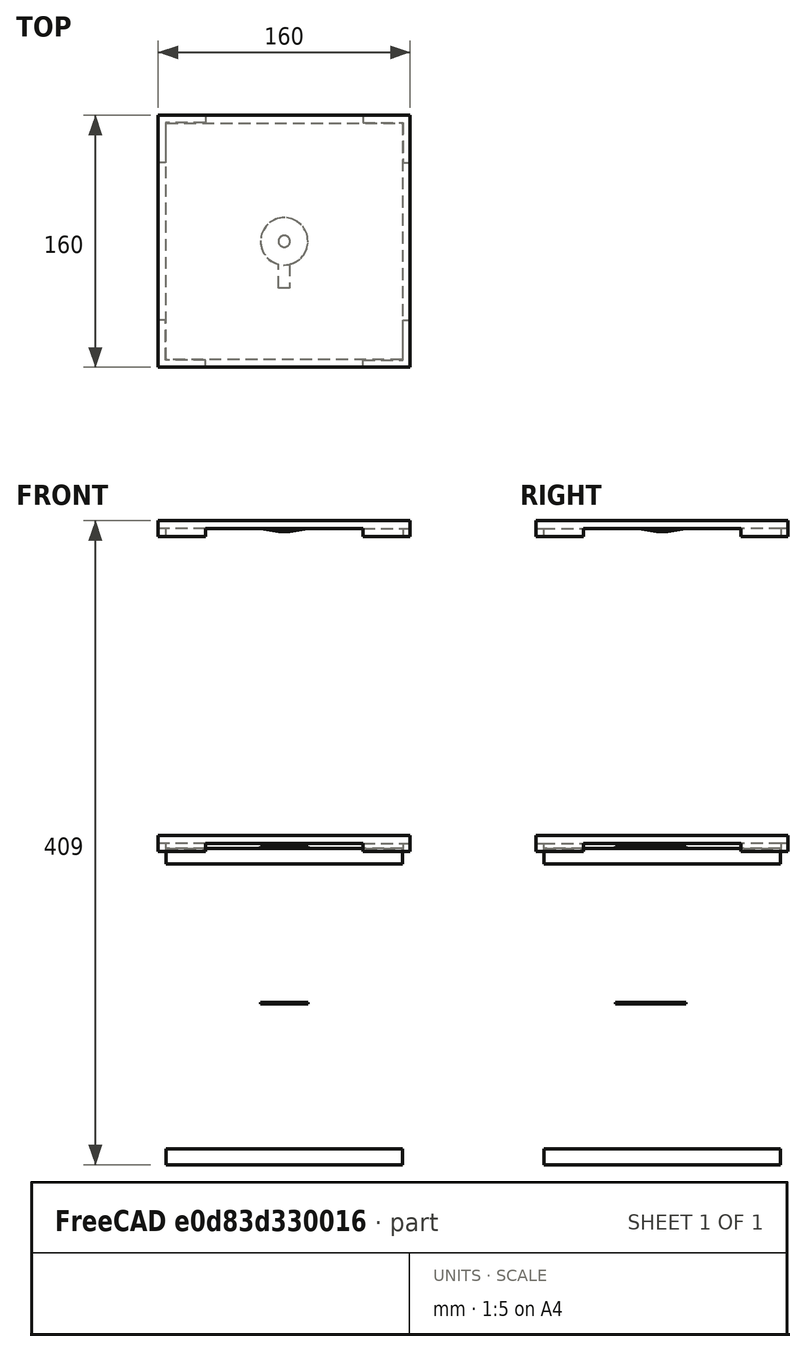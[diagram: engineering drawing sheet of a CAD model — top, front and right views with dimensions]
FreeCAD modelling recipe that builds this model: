
FCSTD DOCUMENT  (FreeCAD 0.21R33771 (Git))
Label: Pedle
License: All rights reserved
LicenseURL: https://en.wikipedia.org/wiki/All_rights_reserved
objects: Sketcher::SketchObject×10, PartDesign::Pad×10, TechDraw::DrawProjGroupItem×10, TechDraw::DrawViewDimension×10, PartDesign::Body×6, Part::Mirroring×6, TechDraw::DrawProjGroup×4, TechDraw::DrawSVGTemplate×3, TechDraw::DrawPage×3, TechDraw::DrawViewBalloon×3, App::DocumentObjectGroupPython×3, PartDesign::Draft×2, Part::MultiFuse×2, App::Part×2, Part::Feature×2, Spreadsheet::Sheet×1, TechDraw::DrawViewSpreadsheet×1
note: 67 computed .brp shape members not serialized (recipe doc carries the construction recipe); baked Part::Feature solids carry a one-line shape summary decoded from their .brp

FEATURE [Sketcher::SketchObject] Sketch
  FullyConstrained = true
  MapMode = 5
  Support = -> [XY_Plane]
  sketch-geometry (5):
    g0: LineSegment StartX=-75 StartY=-75 StartZ=0 EndX=-75 EndY=75 EndZ=0
    g1: LineSegment StartX=-75 StartY=75 StartZ=0 EndX=75 EndY=75 EndZ=0
    g2: LineSegment StartX=75 StartY=75 StartZ=0 EndX=75 EndY=-75 EndZ=0
    g3: LineSegment StartX=75 StartY=-75 StartZ=0 EndX=-75 EndY=-75 EndZ=0
    g4: GeomPoint X=-6e-16 Y=0 Z=0
  constraints (12):
    c: Coincident(g0,g1)
    c: Coincident(g1,g2)
    c: Coincident(g2,g3)
    c: Coincident(g3,g0)
    c: Horizontal(g1)
    c: Horizontal(g3)
    c: Vertical(g0)
    c: Vertical(g2)
    c: Symmetric(g1,g0,g4)
    c: Coincident(g4,g-1)
    c: Equal(g1,g2)
    c: DistanceX(g1,g1) = 150
FEATURE [PartDesign::Pad] Pad
  Direction = (0,0,1)
  Length = 10
  Length2 = 10
  Profile = -> Sketch
  ReferenceAxis = -> Sketch [N_Axis]
  Reversed = true
  Type = 0
FEATURE [PartDesign::Body] Body  label="Foam"
  Group = -> [Sketch,Pad]
  Origin = -> Origin
  Placement = pos=(0,0,-3) rot=(0,0,1;0rad)
  Tip = -> Pad
FEATURE [Sketcher::SketchObject] Sketch001
  FullyConstrained = true
  MapMode = 5
  Support = -> [XY_Plane001]
  sketch-geometry (4):
    g0: LineSegment StartX=-80 StartY=0 StartZ=0 EndX=-80 EndY=80 EndZ=0
    g1: LineSegment StartX=-80 StartY=80 StartZ=0 EndX=0 EndY=80 EndZ=0
    g2: LineSegment StartX=0 StartY=80 StartZ=0 EndX=0 EndY=0 EndZ=0
    g3: LineSegment StartX=0 StartY=0 StartZ=0 EndX=-80 EndY=0 EndZ=0
  constraints (11):
    c: Coincident(g0,g1)
    c: Coincident(g1,g2)
    c: Coincident(g2,g3)
    c: Coincident(g3,g0)
    c: Horizontal(g1)
    c: Horizontal(g3)
    c: Vertical(g0)
    c: Vertical(g2)
    c: DistanceX(g1,g1) = 80
    c: Equal(g2,g1)
    c: Coincident(g2,g-1)
FEATURE [PartDesign::Pad] Pad001
  Direction = (0,0,1)
  Length = 5
  Length2 = 10
  Profile = -> Sketch001
  ReferenceAxis = -> Sketch001 [N_Axis]
  Type = 0
FEATURE [Sketcher::SketchObject] Sketch002
  FullyConstrained = true
  MapMode = 5
  Support = -> [XY_Plane001]
  expr: Constraints[11] = Sketch.Constraints[11]
  expr: Constraints[20] = Sketch001.Constraints[8]
  sketch-geometry (15):
    g0: LineSegment StartX=-75 StartY=-75 StartZ=0 EndX=-75 EndY=75 EndZ=0
    g1: LineSegment StartX=-75 StartY=75 StartZ=0 EndX=75 EndY=75 EndZ=0
    g2: LineSegment StartX=75 StartY=75 StartZ=0 EndX=75 EndY=-75 EndZ=0
    g3: LineSegment StartX=75 StartY=-75 StartZ=0 EndX=-75 EndY=-75 EndZ=0
    g4: GeomPoint X=0 Y=0 Z=0
    g5: LineSegment StartX=-80 StartY=0 StartZ=0 EndX=-80 EndY=80 EndZ=0
    g6: LineSegment StartX=-80 StartY=80 StartZ=0 EndX=0 EndY=80 EndZ=0
    g7: LineSegment StartX=0 StartY=80 StartZ=0 EndX=0 EndY=0 EndZ=0
    g8: LineSegment StartX=0 StartY=0 StartZ=0 EndX=-80 EndY=0 EndZ=0
    g9: LineSegment StartX=-80 StartY=80 StartZ=0 EndX=-50 EndY=80 EndZ=0
    g10: LineSegment StartX=-50 StartY=80 StartZ=0 EndX=-50 EndY=75.4 EndZ=0
    g11: LineSegment StartX=-50 StartY=75.4 StartZ=0 EndX=-75.4 EndY=75.4 EndZ=0
    g12: LineSegment StartX=-75.4 StartY=75.4 StartZ=0 EndX=-75.4 EndY=50 EndZ=0
    g13: LineSegment StartX=-75.4 StartY=50 StartZ=0 EndX=-80 EndY=50 EndZ=0
    g14: LineSegment StartX=-80 StartY=50 StartZ=0 EndX=-80 EndY=80 EndZ=0
  constraints (40):
    c: Coincident(g0,g1)
    c: Coincident(g1,g2)
    c: Coincident(g2,g3)
    c: Coincident(g3,g0)
    c: Horizontal(g1)
    c: Horizontal(g3)
    c: Vertical(g0)
    c: Vertical(g2)
    c: Symmetric(g1,g0,g4)
    c: Coincident(g4,g-1)
    c: Equal(g1,g2)
    c: DistanceX(g1,g1) = 150
    c: Coincident(g5,g6)
    c: Coincident(g6,g7)
    c: Coincident(g7,g8)
    c: Coincident(g8,g5)
    c: Horizontal(g6)
    c: Horizontal(g8)
    c: Vertical(g5)
    c: Vertical(g7)
    c: DistanceX(g6,g6) = 80
    c: Equal(g7,g6)
    c: Coincident(g7,g-1)
    c: Coincident(g9,g5)
    c: PointOnObject(g9,g6)
    c: Coincident(g10,g9)
    c: Vertical(g10)
    c: Coincident(g11,g10)
    c: Horizontal(g11)
    c: Coincident(g12,g11)
    c: Vertical(g12)
    c: Coincident(g13,g12)
    c: PointOnObject(g13,g5)
    c: Horizontal(g13)
    c: Coincident(g14,g13)
    c: Coincident(g14,g9)
    c: Equal(g9,g14)
    c: Equal(g13,g10)
    c: DistanceX(g11,g0) = 0.4
    c: DistanceX(g9,g9) = 30
FEATURE [PartDesign::Pad] Pad002
  BaseFeature = -> Pad001
  Direction = (0,0,1)
  Length = 5
  Length2 = 10
  Profile = -> Sketch002
  ReferenceAxis = -> Sketch002 [N_Axis]
  Reversed = true
  Type = 0
  expr: Length = 5
FEATURE [Sketcher::SketchObject] Sketch003
  FullyConstrained = true
  MapMode = 5
  Support = -> [XY_Plane001]
  sketch-geometry (3):
    g0: ArcOfCircle CenterX=0 CenterY=0 CenterZ=0 NormalX=0 NormalY=0 NormalZ=1 AngleXU=0 Radius=15 StartAngle=1.5708 EndAngle=3.14159
    g1: LineSegment StartX=9e-16 StartY=15 StartZ=0 EndX=0 EndY=0 EndZ=0
    g2: LineSegment StartX=0 StartY=0 StartZ=0 EndX=-15 EndY=1.8e-15 EndZ=0
  constraints (8):
    c: Coincident(g0,g-1)
    c: PointOnObject(g0,g-2)
    c: PointOnObject(g0,g-1)
    c: Radius(g0) = 15
    c: Coincident(g1,g0)
    c: Coincident(g1,g0)
    c: Coincident(g2,g0)
    c: Coincident(g2,g0)
FEATURE [PartDesign::Pad] Pad003
  BaseFeature = -> Pad002
  Direction = (0,0,1)
  Length = 2
  Length2 = 10
  Profile = -> Sketch003
  ReferenceAxis = -> Sketch003 [N_Axis]
  Reversed = true
  Type = 0
FEATURE [PartDesign::Draft] Draft
  Angle = 80
  Base = -> Pad003 [Face14]
  BaseFeature = -> Pad003
  NeutralPlane = -> Pad003 [Face4]
  Reversed = true
  SupportTransform = false
FEATURE [PartDesign::Body] Body001  label="HardPart"
  Group = -> [Sketch001,Pad001,Sketch002,Pad002,Sketch003,Pad003,Draft]
  Origin = -> Origin001
  Tip = -> Draft
FEATURE [Part::Mirroring] Part__Mirroring  label="HardPart (Mirror #1)"
  Base = (0,0,0)
  Normal = (0,1,0)
  Source = -> Body001
FEATURE [Part::Mirroring] Part__Mirroring001  label="HardPart (Mirror #2)"
  Base = (0,0,0)
  Normal = (1,0,0)
  Source = -> Part__Mirroring
FEATURE [Part::Mirroring] Part__Mirroring002  label="HardPart (Mirror #3)"
  Base = (0,0,0)
  Normal = (1,0,0)
  Source = -> Body001
FEATURE [Part::MultiFuse] Fusion
  Placement = pos=(0,0,200) rot=(0,0,1;0rad)
  Shapes = -> [Part__Mirroring,Part__Mirroring001,Part__Mirroring002,Body001]
FEATURE [Sketcher::SketchObject] Sketch004
  FullyConstrained = true
  MapMode = 5
  Support = -> [XY_Plane002]
  sketch-geometry (4):
    g0: ArcOfCircle CenterX=0 CenterY=0 CenterZ=0 NormalX=0 NormalY=0 NormalZ=1 AngleXU=0 Radius=15 StartAngle=4.94789 EndAngle=10.7601
    g1: LineSegment StartX=3.5 StartY=-14.586 StartZ=0 EndX=3.5 EndY=-29.586 EndZ=0
    g2: LineSegment StartX=3.5 StartY=-29.586 StartZ=0 EndX=-3.5 EndY=-29.586 EndZ=0
    g3: LineSegment StartX=-3.5 StartY=-29.586 StartZ=0 EndX=-3.5 EndY=-14.586 EndZ=0
  constraints (11):
    c: Coincident(g0,g-1)
    c: Coincident(g1,g0)
    c: Vertical(g1)
    c: Coincident(g2,g1)
    c: Coincident(g3,g2)
    c: Coincident(g3,g0)
    c: Vertical(g3)
    c: Symmetric(g1,g2,g-2)
    c: Radius(g0) = 15
    c: DistanceY(g1,g1) = 15
    c: DistanceX(g2,g2) = 7
FEATURE [PartDesign::Pad] Pad004
  Direction = (0,0,1)
  Length = 1
  Length2 = 10
  Placement = pos=(0,0,100) rot=(0,0,1;0rad)
  Profile = -> Sketch004
  ReferenceAxis = -> Sketch004 [N_Axis]
  Type = 0
FEATURE [PartDesign::Body] Body002  label="Sensor"
  Group = -> [Sketch004,Pad004]
  Origin = -> Origin002
  Placement = pos=(0,0,-3) rot=(0,0,1;0rad)
  Tip = -> Pad004
FEATURE [TechDraw::DrawSVGTemplate] Template
  EditableTexts = AuthorName=Alex Anastasakis; CheckDate=2024/11/11; CreationDate=2024/11/11; DrawingNumber=1; FC-Scale=1:2; FC-Title=Plate; SheetNumber=1 of 1; Subtitle=Course: Industrial Design for Game Hardware; SupervisorName=Alvaro Uribe Quevedo; Weight=0.09
  Height = 297
  Orientation = 1
  Template = C:/Program Files/FreeCAD 0.21/data/Mod/TechDraw/Templates/A3_LandscapeTD.svg
  Width = 420
FEATURE [TechDraw::DrawProjGroupItem] ProjItem  label="Front"
  CoarseView = false
  Direction = (0,-1,0)
  Focus = 100
  HardHidden = false
  IsoCount = 0
  IsoHidden = false
  IsoVisible = false
  LockPosition = true
  Perspective = false
  Rotation = 0
  RotationVector = (1,0,0)
  Scale = 0.5
  ScaleType = 2
  ScrubCount = 0
  SeamHidden = false
  SeamVisible = false
  SmoothHidden = false
  SmoothVisible = true
  Source = -> [Fusion]
  Type = 0
  X = 0
  XDirection = (1,0,0)
  Y = 0
FEATURE [TechDraw::DrawProjGroupItem] ProjItem001  label="Bottom"
  CoarseView = false
  Direction = (0,0,-1)
  Focus = 100
  HardHidden = false
  IsoCount = 0
  IsoHidden = false
  IsoVisible = false
  LockPosition = false
  Perspective = false
  Rotation = 0
  RotationVector = (1,0,0)
  Scale = 0.5
  ScaleType = 2
  ScrubCount = 0
  SeamHidden = false
  SeamVisible = false
  SmoothHidden = false
  SmoothVisible = true
  Source = -> [Fusion]
  Type = 5
  X = 0
  XDirection = (1,0,0)
  Y = -72.5
FEATURE [TechDraw::DrawViewDimension] Dimension002
  AngleOverride = false
  Arbitrary = false
  ArbitraryTolerances = false
  EqualTolerance = true
  ExtensionAngle = 0
  FormatSpec = ⌀%.2w
  FormatSpecOverTolerance = %+.2w
  FormatSpecUnderTolerance = %+.2w
  Inverted = false
  LineAngle = 0
  LockPosition = false
  MeasureType = 1
  OverTolerance = 0
  References2D = -> [ProjItem001]
  Rotation = 0
  Scale = 0.5
  ScaleType = 0
  TheoreticalExact = false
  Type = 5
  UnderTolerance = 0
  X = 51.6169
  Y = 21.7849
FEATURE [TechDraw::DrawViewDimension] Dimension003
  AngleOverride = false
  Arbitrary = false
  ArbitraryTolerances = false
  EqualTolerance = true
  ExtensionAngle = 0
  FormatSpec = %.2w
  FormatSpecOverTolerance = %+.2w
  FormatSpecUnderTolerance = %+.2w
  Inverted = false
  LineAngle = 0
  LockPosition = false
  MeasureType = 1
  OverTolerance = 0
  References2D = -> [ProjItem]
  Rotation = 0
  Scale = 0.5
  ScaleType = 0
  TheoreticalExact = false
  Type = 2
  UnderTolerance = 0
  X = -57.1938
  Y = 16.266
FEATURE [TechDraw::DrawViewDimension] Dimension004
  AngleOverride = false
  Arbitrary = false
  ArbitraryTolerances = false
  EqualTolerance = true
  ExtensionAngle = 0
  FormatSpec = %.2w
  FormatSpecOverTolerance = %+.2w
  FormatSpecUnderTolerance = %+.2w
  Inverted = false
  LineAngle = 0
  LockPosition = false
  MeasureType = 1
  OverTolerance = 0
  References2D = -> [ProjItem]
  Rotation = 0
  Scale = 0.5
  ScaleType = 0
  TheoreticalExact = false
  Type = 2
  UnderTolerance = 0
  X = -48.3522
  Y = 16.1652
FEATURE [TechDraw::DrawViewDimension] Dimension005
  AngleOverride = false
  Arbitrary = false
  ArbitraryTolerances = false
  EqualTolerance = true
  ExtensionAngle = 0
  FormatSpec = %.2w x80°
  FormatSpecOverTolerance = %+.2w
  FormatSpecUnderTolerance = %+.2w
  Inverted = false
  LineAngle = 0
  LockPosition = false
  MeasureType = 1
  OverTolerance = 0
  References2D = -> [ProjItem]
  Rotation = 0
  Scale = 0.5
  ScaleType = 0
  TheoreticalExact = false
  Type = 2
  UnderTolerance = 0
  X = 52.4746
  Y = 12.9587
FEATURE [TechDraw::DrawProjGroupItem] ProjItem002  label="FrontTopRight"
  CoarseView = false
  Direction = (0.57735,-0.57735,0.57735)
  Focus = 100
  HardHidden = false
  IsoCount = 0
  IsoHidden = false
  IsoVisible = false
  LockPosition = false
  Perspective = false
  Rotation = 0
  RotationVector = (1,0,0)
  ScaleType = 2
  ScrubCount = 0
  SeamHidden = false
  SeamVisible = false
  SmoothHidden = false
  SmoothVisible = true
  Source = -> [Fusion]
  Type = 7
  X = 126.569
  XDirection = (0.707107,0.707107,0)
  Y = 72.5
FEATURE [TechDraw::DrawProjGroupItem] ProjItem003  label="Top"
  CoarseView = false
  Direction = (0,0,1)
  Focus = 100
  HardHidden = false
  IsoCount = 0
  IsoHidden = false
  IsoVisible = false
  LockPosition = false
  Perspective = false
  Rotation = 0
  RotationVector = (1,0,0)
  ScaleType = 2
  ScrubCount = 0
  SeamHidden = false
  SeamVisible = false
  SmoothHidden = false
  SmoothVisible = true
  Source = -> [Fusion]
  Type = 4
  X = 0
  XDirection = (1,0,0)
  Y = 72.5
FEATURE [TechDraw::DrawProjGroup] ProjGroup
  Anchor = -> ProjItem
  AutoDistribute = true
  LockPosition = false
  ProjectionType = 1
  Rotation = 0
  Scale = 0.5
  ScaleType = 0
  Source = -> [Fusion]
  Views = -> [ProjItem,ProjItem001,ProjItem002,ProjItem003]
  X = 155.738
  Y = 152.297
  spacingX = 30
  spacingY = 30
FEATURE [TechDraw::DrawViewDimension] Dimension
  AngleOverride = false
  Arbitrary = false
  ArbitraryTolerances = false
  EqualTolerance = true
  ExtensionAngle = 0
  FormatSpec = %.2w
  FormatSpecOverTolerance = %+.2w
  FormatSpecUnderTolerance = %+.2w
  Inverted = false
  LineAngle = 0
  LockPosition = false
  MeasureType = 1
  OverTolerance = 0
  References2D = -> [ProjItem003]
  Rotation = 0
  Scale = 0.5
  ScaleType = 0
  TheoreticalExact = false
  Type = 1
  UnderTolerance = 0
  X = -0.816766
  Y = 56.5615
FEATURE [TechDraw::DrawViewDimension] Dimension006
  AngleOverride = false
  Arbitrary = false
  ArbitraryTolerances = false
  EqualTolerance = true
  ExtensionAngle = 0
  FormatSpec = %.2w
  FormatSpecOverTolerance = %+.2w
  FormatSpecUnderTolerance = %+.2w
  Inverted = false
  LineAngle = 0
  LockPosition = false
  MeasureType = 1
  OverTolerance = 0
  References2D = -> [ProjItem003]
  Rotation = 0
  Scale = 0.5
  ScaleType = 0
  TheoreticalExact = false
  Type = 2
  UnderTolerance = 0
  X = -53.9399
  Y = 2.24418
FEATURE [TechDraw::DrawViewDimension] Dimension007
  AngleOverride = false
  Arbitrary = false
  ArbitraryTolerances = false
  EqualTolerance = true
  ExtensionAngle = 0
  FormatSpec = %.2w
  FormatSpecOverTolerance = %+.2w
  FormatSpecUnderTolerance = %+.2w
  Inverted = false
  LineAngle = 0
  LockPosition = false
  MeasureType = 1
  OverTolerance = 0
  References2D = -> [ProjItem001]
  Rotation = 0
  Scale = 0.5
  ScaleType = 0
  TheoreticalExact = false
  Type = 1
  UnderTolerance = 0
  X = -51.8082
  Y = 18.2692
FEATURE [TechDraw::DrawViewDimension] Dimension008
  AngleOverride = false
  Arbitrary = false
  ArbitraryTolerances = false
  EqualTolerance = true
  ExtensionAngle = 0
  FormatSpec = %.2w
  FormatSpecOverTolerance = %+.2w
  FormatSpecUnderTolerance = %+.2w
  Inverted = false
  LineAngle = 0
  LockPosition = false
  MeasureType = 1
  OverTolerance = 0
  References2D = -> [ProjItem001]
  Rotation = 0
  Scale = 0.5
  ScaleType = 0
  TheoreticalExact = false
  Type = 2
  UnderTolerance = 0
  X = -14.7786
  Y = 52.5746
FEATURE [TechDraw::DrawViewDimension] Dimension009
  AngleOverride = false
  Arbitrary = false
  ArbitraryTolerances = false
  EqualTolerance = true
  ExtensionAngle = 0
  FormatSpec = %.2w
  FormatSpecOverTolerance = %+.2w
  FormatSpecUnderTolerance = %+.2w
  Inverted = false
  LineAngle = 0
  LockPosition = false
  MeasureType = 1
  OverTolerance = 0
  References2D = -> [ProjItem001]
  Rotation = 0
  Scale = 0.5
  ScaleType = 0
  TheoreticalExact = false
  Type = 2
  UnderTolerance = 0
  X = -59.7622
  Y = 10.7657
FEATURE [TechDraw::DrawViewDimension] Dimension010
  AngleOverride = false
  Arbitrary = false
  ArbitraryTolerances = false
  EqualTolerance = true
  ExtensionAngle = 0
  FormatSpec = %.2w
  FormatSpecOverTolerance = %+.2w
  FormatSpecUnderTolerance = %+.2w
  Inverted = false
  LineAngle = 0
  LockPosition = false
  MeasureType = 1
  OverTolerance = 0
  References2D = -> [ProjItem001]
  Rotation = 0
  Scale = 0.5
  ScaleType = 0
  TheoreticalExact = false
  Type = 1
  UnderTolerance = 0
  X = -5.20054
  Y = 58.7965
FEATURE [TechDraw::DrawPage] Page
  KeepUpdated = true
  NextBalloonIndex = 1
  ProjectionType = 0
  Scale = 0.5
  Template = -> Template
  Views = -> [ProjGroup,Dimension002,Dimension003,Dimension004,Dimension005,Dimension,Dimension006,Dimension007,Dimension008,Dimension009,Dimension010]
FEATURE [App::Part] Part  label="Pedal"
  Group = -> [Body,Part__Mirroring002,Part__Mirroring001,Part__Mirroring,Body001,Fusion,Body002]
  Origin = -> Origin003
FEATURE [Sketcher::SketchObject] Sketch005
  FullyConstrained = true
  MapMode = 5
  Support = -> [XY_Plane004]
  sketch-geometry (5):
    g0: LineSegment StartX=-75 StartY=-75 StartZ=0 EndX=-75 EndY=75 EndZ=0
    g1: LineSegment StartX=-75 StartY=75 StartZ=0 EndX=75 EndY=75 EndZ=0
    g2: LineSegment StartX=75 StartY=75 StartZ=0 EndX=75 EndY=-75 EndZ=0
    g3: LineSegment StartX=75 StartY=-75 StartZ=0 EndX=-75 EndY=-75 EndZ=0
    g4: GeomPoint X=-6e-16 Y=0 Z=0
  constraints (12):
    c: Coincident(g0,g1)
    c: Coincident(g1,g2)
    c: Coincident(g2,g3)
    c: Coincident(g3,g0)
    c: Horizontal(g1)
    c: Horizontal(g3)
    c: Vertical(g0)
    c: Vertical(g2)
    c: Symmetric(g1,g0,g4)
    c: Coincident(g4,g-1)
    c: Equal(g1,g2)
    c: DistanceX(g1,g1) = 150
FEATURE [PartDesign::Pad] Pad005
  Direction = (0,0,1)
  Length = 10
  Length2 = 10
  Profile = -> Sketch005
  ReferenceAxis = -> Sketch005 [N_Axis]
  Reversed = true
  Type = 0
FEATURE [PartDesign::Body] Body003  label="Foam001"
  Group = -> [Sketch005,Pad005]
  Origin = -> Origin004
  Placement = pos=(0,0,-194) rot=(0,0,1;0rad)
  Tip = -> Pad005
FEATURE [Sketcher::SketchObject] Sketch006
  FullyConstrained = true
  MapMode = 5
  Support = -> [XY_Plane005]
  sketch-geometry (4):
    g0: LineSegment StartX=-80 StartY=0 StartZ=0 EndX=-80 EndY=80 EndZ=0
    g1: LineSegment StartX=-80 StartY=80 StartZ=0 EndX=0 EndY=80 EndZ=0
    g2: LineSegment StartX=0 StartY=80 StartZ=0 EndX=0 EndY=0 EndZ=0
    g3: LineSegment StartX=0 StartY=0 StartZ=0 EndX=-80 EndY=0 EndZ=0
  constraints (11):
    c: Coincident(g0,g1)
    c: Coincident(g1,g2)
    c: Coincident(g2,g3)
    c: Coincident(g3,g0)
    c: Horizontal(g1)
    c: Horizontal(g3)
    c: Vertical(g0)
    c: Vertical(g2)
    c: DistanceX(g1,g1) = 80
    c: Equal(g2,g1)
    c: Coincident(g2,g-1)
FEATURE [PartDesign::Pad] Pad006
  Direction = (0,0,1)
  Length = 5
  Length2 = 10
  Profile = -> Sketch006
  ReferenceAxis = -> Sketch006 [N_Axis]
  Type = 0
FEATURE [Sketcher::SketchObject] Sketch007
  FullyConstrained = true
  MapMode = 5
  Support = -> [XY_Plane005]
  expr: Constraints[11] = Sketch005.Constraints[11]
  expr: Constraints[20] = Sketch006.Constraints[8]
  sketch-geometry (15):
    g0: LineSegment StartX=-75 StartY=-75 StartZ=0 EndX=-75 EndY=75 EndZ=0
    g1: LineSegment StartX=-75 StartY=75 StartZ=0 EndX=75 EndY=75 EndZ=0
    g2: LineSegment StartX=75 StartY=75 StartZ=0 EndX=75 EndY=-75 EndZ=0
    g3: LineSegment StartX=75 StartY=-75 StartZ=0 EndX=-75 EndY=-75 EndZ=0
    g4: GeomPoint X=0 Y=0 Z=0
    g5: LineSegment StartX=-80 StartY=0 StartZ=0 EndX=-80 EndY=80 EndZ=0
    g6: LineSegment StartX=-80 StartY=80 StartZ=0 EndX=0 EndY=80 EndZ=0
    g7: LineSegment StartX=0 StartY=80 StartZ=0 EndX=0 EndY=0 EndZ=0
    g8: LineSegment StartX=0 StartY=0 StartZ=0 EndX=-80 EndY=0 EndZ=0
    g9: LineSegment StartX=-80 StartY=80 StartZ=0 EndX=-50 EndY=80 EndZ=0
    g10: LineSegment StartX=-50 StartY=80 StartZ=0 EndX=-50 EndY=75.4 EndZ=0
    g11: LineSegment StartX=-50 StartY=75.4 StartZ=0 EndX=-75.4 EndY=75.4 EndZ=0
    g12: LineSegment StartX=-75.4 StartY=75.4 StartZ=0 EndX=-75.4 EndY=50 EndZ=0
    g13: LineSegment StartX=-75.4 StartY=50 StartZ=0 EndX=-80 EndY=50 EndZ=0
    g14: LineSegment StartX=-80 StartY=50 StartZ=0 EndX=-80 EndY=80 EndZ=0
  constraints (40):
    c: Coincident(g0,g1)
    c: Coincident(g1,g2)
    c: Coincident(g2,g3)
    c: Coincident(g3,g0)
    c: Horizontal(g1)
    c: Horizontal(g3)
    c: Vertical(g0)
    c: Vertical(g2)
    c: Symmetric(g1,g0,g4)
    c: Coincident(g4,g-1)
    c: Equal(g1,g2)
    c: DistanceX(g1,g1) = 150
    c: Coincident(g5,g6)
    c: Coincident(g6,g7)
    c: Coincident(g7,g8)
    c: Coincident(g8,g5)
    c: Horizontal(g6)
    c: Horizontal(g8)
    c: Vertical(g5)
    c: Vertical(g7)
    c: DistanceX(g6,g6) = 80
    c: Equal(g7,g6)
    c: Coincident(g7,g-1)
    c: Coincident(g9,g5)
    c: PointOnObject(g9,g6)
    c: Coincident(g10,g9)
    c: Vertical(g10)
    c: Coincident(g11,g10)
    c: Horizontal(g11)
    c: Coincident(g12,g11)
    c: Vertical(g12)
    c: Coincident(g13,g12)
    c: PointOnObject(g13,g5)
    c: Horizontal(g13)
    c: Coincident(g14,g13)
    c: Coincident(g14,g9)
    c: Equal(g9,g14)
    c: Equal(g13,g10)
    c: DistanceX(g11,g0) = 0.4
    c: DistanceX(g9,g9) = 30
FEATURE [PartDesign::Pad] Pad007
  BaseFeature = -> Pad006
  Direction = (0,0,1)
  Length = 5
  Length2 = 10
  Profile = -> Sketch007
  ReferenceAxis = -> Sketch007 [N_Axis]
  Reversed = true
  Type = 0
  expr: Length = 5
FEATURE [Sketcher::SketchObject] Sketch008
  FullyConstrained = true
  MapMode = 5
  Support = -> [XY_Plane005]
  sketch-geometry (3):
    g0: ArcOfCircle CenterX=0 CenterY=0 CenterZ=0 NormalX=0 NormalY=0 NormalZ=1 AngleXU=0 Radius=15 StartAngle=1.5708 EndAngle=3.14159
    g1: LineSegment StartX=9e-16 StartY=15 StartZ=0 EndX=0 EndY=0 EndZ=0
    g2: LineSegment StartX=0 StartY=0 StartZ=0 EndX=-15 EndY=1.8e-15 EndZ=0
  constraints (8):
    c: Coincident(g0,g-1)
    c: PointOnObject(g0,g-2)
    c: PointOnObject(g0,g-1)
    c: Radius(g0) = 15
    c: Coincident(g1,g0)
    c: Coincident(g1,g0)
    c: Coincident(g2,g0)
    c: Coincident(g2,g0)
FEATURE [PartDesign::Pad] Pad008
  BaseFeature = -> Pad007
  Direction = (0,0,1)
  Length = 2
  Length2 = 10
  Profile = -> Sketch008
  ReferenceAxis = -> Sketch008 [N_Axis]
  Reversed = true
  Type = 0
FEATURE [PartDesign::Draft] Draft001
  Angle = 80
  Base = -> Pad008 [Face14]
  BaseFeature = -> Pad008
  NeutralPlane = -> Pad008 [Face4]
  Reversed = true
  SupportTransform = false
FEATURE [PartDesign::Body] Body004  label="HardPart001"
  Group = -> [Sketch006,Pad006,Sketch007,Pad007,Sketch008,Pad008,Draft001]
  Origin = -> Origin005
  Tip = -> Draft001
FEATURE [Part::Mirroring] Part__Mirroring003  label="HardPart (Mirror #1)001"
  Base = (0,0,0)
  Normal = (0,1,0)
  Source = -> Body004
FEATURE [Part::Mirroring] Part__Mirroring004  label="HardPart (Mirror #2)001"
  Base = (0,0,0)
  Normal = (1,0,0)
  Source = -> Part__Mirroring003
FEATURE [Part::Mirroring] Part__Mirroring005  label="HardPart (Mirror #3)001"
  Base = (0,0,0)
  Normal = (1,0,0)
  Source = -> Body004
FEATURE [Part::MultiFuse] Fusion001
  Shapes = -> [Part__Mirroring003,Part__Mirroring004,Part__Mirroring005,Body004]
FEATURE [Sketcher::SketchObject] Sketch009
  FullyConstrained = true
  MapMode = 5
  Support = -> [XY_Plane006]
  sketch-geometry (4):
    g0: ArcOfCircle CenterX=0 CenterY=0 CenterZ=0 NormalX=0 NormalY=0 NormalZ=1 AngleXU=0 Radius=15 StartAngle=4.94789 EndAngle=10.7601
    g1: LineSegment StartX=3.5 StartY=-14.586 StartZ=0 EndX=3.5 EndY=-29.586 EndZ=0
    g2: LineSegment StartX=3.5 StartY=-29.586 StartZ=0 EndX=-3.5 EndY=-29.586 EndZ=0
    g3: LineSegment StartX=-3.5 StartY=-29.586 StartZ=0 EndX=-3.5 EndY=-14.586 EndZ=0
  constraints (11):
    c: Coincident(g0,g-1)
    c: Coincident(g1,g0)
    c: Vertical(g1)
    c: Coincident(g2,g1)
    c: Coincident(g3,g2)
    c: Coincident(g3,g0)
    c: Vertical(g3)
    c: Symmetric(g1,g2,g-2)
    c: Radius(g0) = 15
    c: DistanceY(g1,g1) = 15
    c: DistanceX(g2,g2) = 7
FEATURE [PartDesign::Pad] Pad009
  Direction = (0,0,1)
  Length = 1
  Length2 = 10
  Profile = -> Sketch009
  ReferenceAxis = -> Sketch009 [N_Axis]
  Type = 0
FEATURE [PartDesign::Body] Body005  label="Sensor001"
  Group = -> [Sketch009,Pad009]
  Origin = -> Origin006
  Placement = pos=(0,0,-102) rot=(0,0,1;0rad)
  Tip = -> Pad009
FEATURE [App::Part] Part001  label="PedalExploded"
  Group = -> [Body003,Part__Mirroring005,Part__Mirroring004,Part__Mirroring003,Body004,Fusion001,Body005]
  Origin = -> Origin007
FEATURE [TechDraw::DrawSVGTemplate] Template001
  EditableTexts = AuthorName=Alex Anastasakis; CheckDate=2024/11/11; CreationDate=2024/11/11; FC-Scale=1:2; FC-Title=Pedal; SheetNumber=1 of 1; Subtitle=Course: Industrial Design for Game Hardware; SupervisorName=Alvaro Uribe Quevedo
  Height = 297
  Orientation = 1
  Template = C:/Program Files/FreeCAD 0.21/data/Mod/TechDraw/Templates/A3_LandscapeTD.svg
  Width = 420
FEATURE [TechDraw::DrawProjGroupItem] ProjItem004  label="Front001"
  CoarseView = false
  Direction = (0.57735,-0.57735,0.57735)
  Focus = 100
  HardHidden = false
  IsoCount = 0
  IsoHidden = false
  IsoVisible = false
  LockPosition = true
  Perspective = false
  Rotation = 0
  RotationVector = (0.707107,0.707107,0)
  Scale = 0.5
  ScaleType = 2
  ScrubCount = 0
  SeamHidden = false
  SeamVisible = false
  SmoothHidden = false
  SmoothVisible = true
  Source = -> [Part001]
  Type = 0
  X = 0
  XDirection = (0.707107,0.707107,0)
  Y = 0
FEATURE [TechDraw::DrawProjGroup] ProjGroup001
  Anchor = -> ProjItem004
  AutoDistribute = true
  LockPosition = false
  ProjectionType = 1
  Rotation = 0
  Scale = 0.5
  ScaleType = 0
  Source = -> [Part001]
  Views = -> [ProjItem004]
  X = 316.321
  Y = 151.977
  spacingX = 15
  spacingY = 15
FEATURE [Spreadsheet::Sheet] Spreadsheet  label="#BOM#"
  cells = A1='PARTS LIST; A2='ITEM NO.; B2='QTY; C2='NAME; D2='PART DESCRIPTION; E2='MATERIAL; F2='COST; A3=1; B3=1; C3='Plate; D3='Hard surface; E3='PLA; F3='$22.99 (1kg of filament); A4=2; B4=1; C4='Sensor; D4='Force sensor; E4='Plastic/Metal; F4='$14.19; A5=3; B5=1; C5='Foam Pad; D5='Soft foam pad; E5='Polyethylene Foam; F5='$26.99 (pack of sheets)
FEATURE [TechDraw::DrawViewSpreadsheet] Sheet
  CellEnd = F5
  CellStart = A1
  Font = osifont
  LineWidth = 0.5
  LockPosition = false
  Rotation = 0
  ScaleType = 2
  Source = -> Spreadsheet
  Symbol = <blob: 5512 chars omitted>
  TextSize = 12
  X = 331.62
  Y = 267.089
FEATURE [TechDraw::DrawViewBalloon] Balloon
  BubbleShape = 0
  EndType = 0
  EndTypeScale = 1
  KinkLength = 5
  LockPosition = false
  OriginX = 45.5118
  OriginY = 122.624
  Rotation = 0
  Scale = 0.5
  ScaleType = 0
  ShapeScale = 1
  SourceView = -> ProjItem004
  Text = 1
  TextWrapLen = -1
  X = 150.75
  Y = 146.591
FEATURE [TechDraw::DrawViewBalloon] Balloon001
  BubbleShape = 0
  EndType = 0
  EndTypeScale = 1
  KinkLength = 5
  LockPosition = false
  OriginX = 15.1043
  OriginY = -2.32329
  Rotation = 0
  Scale = 0.5
  ScaleType = 0
  ShapeScale = 1
  SourceView = -> ProjItem004
  Text = 2
  TextWrapLen = -1
  X = 154.067
  Y = 31.5952
FEATURE [TechDraw::DrawViewBalloon] Balloon002
  BubbleShape = 0
  EndType = 0
  EndTypeScale = 1
  KinkLength = 5
  LockPosition = false
  OriginX = 68.1792
  OriginY = -57.0569
  Rotation = 0
  Scale = 0.5
  ScaleType = 0
  ShapeScale = 1
  SourceView = -> ProjItem004
  Text = 3
  TextWrapLen = -1
  X = 154.067
  Y = -44.7001
FEATURE [TechDraw::DrawProjGroupItem] ProjItem005  label="Front002"
  CoarseView = false
  Direction = (0,-1,0)
  Focus = 100
  HardHidden = false
  IsoCount = 0
  IsoHidden = false
  IsoVisible = false
  LockPosition = true
  Perspective = false
  Rotation = 0
  RotationVector = (1,0,0)
  ScaleType = 2
  ScrubCount = 0
  SeamHidden = false
  SeamVisible = false
  SmoothHidden = false
  SmoothVisible = true
  Source = -> [Part]
  Type = 0
  X = 0
  XDirection = (1,0,0)
  Y = 0
FEATURE [TechDraw::DrawProjGroupItem] ProjItem006  label="FrontBottomLeft"
  CoarseView = false
  Direction = (-0.57735,-0.57735,-0.57735)
  Focus = 100
  HardHidden = false
  IsoCount = 0
  IsoHidden = false
  IsoVisible = false
  LockPosition = false
  Perspective = false
  Rotation = 0
  RotationVector = (1,0,0)
  ScaleType = 2
  ScrubCount = 0
  SeamHidden = false
  SeamVisible = false
  SmoothHidden = false
  SmoothVisible = true
  Source = -> [Part]
  Type = 8
  X = -111.569
  XDirection = (0.707107,-0.707107,0)
  Y = -54.8135
FEATURE [TechDraw::DrawProjGroupItem] ProjItem007  label="FrontTopLeft"
  CoarseView = false
  Direction = (-0.57735,-0.57735,0.57735)
  Focus = 100
  HardHidden = false
  IsoCount = 0
  IsoHidden = false
  IsoVisible = false
  LockPosition = false
  Perspective = false
  Rotation = 0
  RotationVector = (1,0,0)
  ScaleType = 2
  ScrubCount = 0
  SeamHidden = false
  SeamVisible = false
  SmoothHidden = false
  SmoothVisible = true
  Source = -> [Part]
  Type = 6
  X = -111.569
  XDirection = (0.707107,-0.707107,0)
  Y = 54.8135
FEATURE [TechDraw::DrawProjGroup] ProjGroup002
  Anchor = -> ProjItem005
  AutoDistribute = true
  LockPosition = false
  ProjectionType = 1
  Rotation = 0
  Scale = 0.5
  ScaleType = 0
  Source = -> [Part]
  Views = -> [ProjItem005,ProjItem006,ProjItem007]
  X = 192.784
  Y = 149.92
  spacingX = 15
  spacingY = 15
FEATURE [TechDraw::DrawPage] Page001  label="Exploded"
  KeepUpdated = true
  NextBalloonIndex = 4
  ProjectionType = 0
  Scale = 0.5
  Template = -> Template001
  Views = -> [ProjGroup001,Sheet,Balloon,Balloon001,Balloon002,ProjGroup002]
FEATURE [Part::Feature] trajectory_line
  Placement = pos=(40,40,0) rot=(0,0,1;0rad)
  shape: bbox 2e-07 x 2e-07 x 200 mm, 0 faces, 0 solids (baked)
FEATURE [App::DocumentObjectGroupPython] SimpleGroup  # scripted group (container) (typed FeaturePython)
  AnimationStepTime = 0
  AnimationSteps = 80
  Distance = 200
  Group = -> [trajectory_line]
  Revolutions = 0
  dir_vectors = (1) [(0,0,1)]
  rot_centers = (1) [(-40,-40,5)]
  rot_vectors = (1) [(0,0,1)]
FEATURE [Part::Feature] trajectory_line001
  shape: bbox 2e-07 x 2e-07 x 20 mm, 0 faces, 0 solids (baked)
FEATURE [App::DocumentObjectGroupPython] SimpleGroup001  # scripted group (container) (typed FeaturePython)
  AnimationStepTime = 0
  AnimationSteps = 60
  Distance = 100
  Group = -> [trajectory_line001]
  Revolutions = 0
  dir_vectors = (1) [(0,0,1)]
  rot_centers = (1) [(-2.68016e-16,-2.82798,1)]
  rot_vectors = (1) [(0,0,1)]
FEATURE [App::DocumentObjectGroupPython] ExplodedAssembly  # scripted group (container) (typed FeaturePython)
  AnimationStep = 0
  CurrentTrajectory = -1
  Group = -> [SimpleGroup,SimpleGroup001]
  InAnimation = false
  RemoveAllTrajectories = false
  ResetAnimation = false
FEATURE [TechDraw::DrawSVGTemplate] Template002
  EditableTexts = AuthorName=AUTHOR NAME; CheckDate=CHECK DATE; CreationDate=CREATION DATE; DrawingNumber=NUMBER; FC-Scale=SCALE; FC-Title=TITLE; SheetNumber=SHEET; Subtitle=SUBTITLE; SupervisorName=SUPERVISOR NAME; Weight=WEIGHT
  Height = 297
  Orientation = 1
  Template = C:/Program Files/FreeCAD 0.21/data/Mod/TechDraw/Templates/A3_LandscapeTD.svg
  Width = 420
FEATURE [TechDraw::DrawProjGroupItem] ProjItem008  label="Front003"
  CoarseView = false
  Direction = (0,-1,0)
  Focus = 100
  HardHidden = false
  IsoCount = 0
  IsoHidden = false
  IsoVisible = false
  LockPosition = true
  Perspective = false
  Rotation = 0
  RotationVector = (1,0,0)
  ScaleType = 2
  ScrubCount = 0
  SeamHidden = false
  SeamVisible = false
  SmoothHidden = false
  SmoothVisible = true
  Source = -> [Body]
  Type = 0
  X = 0
  XDirection = (1,0,0)
  Y = 0
FEATURE [TechDraw::DrawProjGroupItem] ProjItem009  label="Bottom001"
  CoarseView = false
  Direction = (0,0,-1)
  Focus = 100
  HardHidden = false
  IsoCount = 0
  IsoHidden = false
  IsoVisible = false
  LockPosition = false
  Perspective = false
  Rotation = 0
  RotationVector = (1,0,0)
  ScaleType = 2
  ScrubCount = 0
  SeamHidden = false
  SeamVisible = false
  SmoothHidden = false
  SmoothVisible = true
  Source = -> [Body]
  Type = 5
  X = 0
  XDirection = (1,0,0)
  Y = -95
FEATURE [TechDraw::DrawProjGroup] ProjGroup003
  Anchor = -> ProjItem008
  AutoDistribute = true
  LockPosition = false
  ProjectionType = 1
  Rotation = 0
  ScaleType = 0
  Source = -> [Body]
  Views = -> [ProjItem008,ProjItem009]
  X = 210
  Y = 148.5
  spacingX = 15
  spacingY = 15
FEATURE [TechDraw::DrawPage] Page002
  KeepUpdated = true
  NextBalloonIndex = 1
  ProjectionType = 0
  Template = -> Template002
  Views = -> [ProjGroup003]
